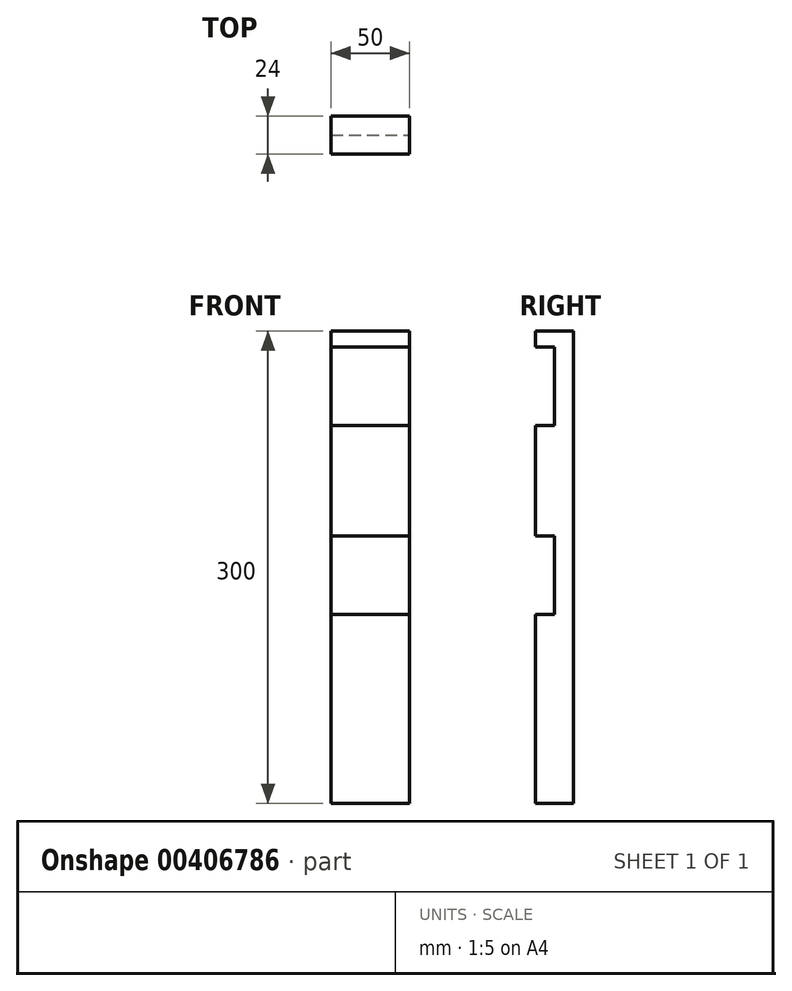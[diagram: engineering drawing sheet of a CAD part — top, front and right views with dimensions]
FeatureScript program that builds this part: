
annotation { "Feature Type Name" : "Feature", "Feature Type Description" : "" }
export const myFeature = defineFeature(function(context is Context, id is Id, definition is map)
    precondition{}
    {
        {
            var Q0;
            Q0=qCreatedBy(makeId("Top.planeOp"),FACE);
            var sketch = newSketch(context, id + "F0", { "sketchPlane" : qUnion([Q0])});
            skLineSegment(sketch, "E0.bottom", {"start": v(25, 12) * mm, "end": v(-25, 12) * mm});
            skLineSegment(sketch, "E0.top", {"start": v(25, -12) * mm, "end": v(-25, -12) * mm});
            skLineSegment(sketch, "E0.left", {"start": v(25, 12) * mm, "end": v(25, -12) * mm});
            skLineSegment(sketch, "E0.right", {"start": v(-25, 12) * mm, "end": v(-25, -12) * mm});
            skPoint(sketch, "E0.middle", {"position": v(0, 0) * mm});
            skSolve(sketch);
        }
        {
            var Q0;
            Q0 = qSketchRegion(id + "F0", true);
            extrude(context, id + "F1", {"entities" : qUnion([Q0]), "depth" : 300 * mm});
        }
        {
            var Q0;
            Q0=makeQuery(id+"F1.opExtrude","SWEPT_FACE",FACE,{"disambiguationData":[OSD([sQuery(id+"F0.wireOp",EDGE,"E0.top")])]});
            var sketch = newSketch(context, id + "F2", { "sketchPlane" : qUnion([Q0])});
            skLineSegment(sketch, "E1.bottom", {"start": v(-25, 290) * mm, "end": v(25, 290) * mm});
            skLineSegment(sketch, "E1.top", {"start": v(-25, 240) * mm, "end": v(25, 240) * mm});
            skLineSegment(sketch, "E1.left", {"start": v(-25, 290) * mm, "end": v(-25, 240) * mm});
            skLineSegment(sketch, "E1.right", {"start": v(25, 290) * mm, "end": v(25, 240) * mm});
            skLineSegment(sketch, "E2.bottom", {"start": v(-25, 170) * mm, "end": v(25, 170) * mm});
            skLineSegment(sketch, "E2.top", {"start": v(-25, 120) * mm, "end": v(25, 120) * mm});
            skLineSegment(sketch, "E2.left", {"start": v(-25, 170) * mm, "end": v(-25, 120) * mm});
            skLineSegment(sketch, "E2.right", {"start": v(25, 170) * mm, "end": v(25, 120) * mm});
            skSolve(sketch);
        }
        {
            var Q0;
            Q0 = qSketchRegion(id + "F2", true);
            extrude(context, id + "F3", {"entities" : qUnion([Q0]), "operationType" : NewBodyOperationType.REMOVE, "oppositeDirection" : true, "depth" : 12 * mm});
        }
    });
